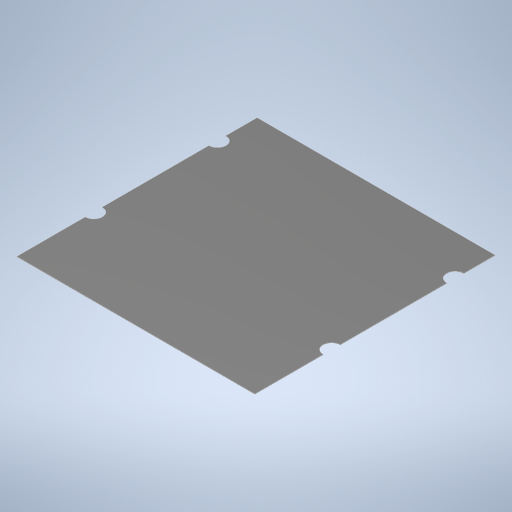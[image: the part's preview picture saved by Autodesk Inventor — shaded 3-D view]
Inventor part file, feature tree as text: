
AUTODESK INVENTOR PART (.ipt)
format: ipt  version: 2023 (Build 270158000, 158)  size: 237,568 bytes
history: native  units: in
note: dims shown in document units (in); Inventor stores cm internally (conversion verified against a paired STEP export)
features: extrude x2, sketch x2
ambient origin geometry x8: Origin, YZ Plane, XZ Plane, XY Plane, X Axis, Y Axis, Z Axis, Center Point
bodies: Solid1 (feature_tree)
feature tree (4):
  extrude  "Extrusion1"  Depth=1.6378in
  extrude  "Extrusion2"  Depth=0.0591in
  sketch  "Sketch1"  dims[d0=1.6535in d1=1.6378in]
  sketch  "Sketch2"  dims[d2=0.0031in d3=0.0in d5=0.0591in d6=0.0in d7=0.0in d8=0.1181in d9=0.2736in d10=0.0591in d11=0.0591in d12=0.0591in d13=1.1244in]
